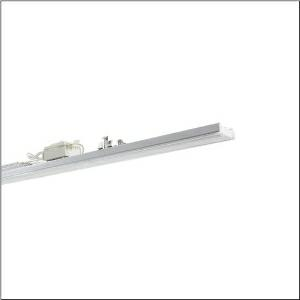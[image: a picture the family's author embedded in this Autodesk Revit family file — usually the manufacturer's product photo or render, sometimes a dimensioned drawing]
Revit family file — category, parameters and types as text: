
# Revit family: licross_r__21_recessed_mo_52tl14dn49xg_3f36
name_source: partatom
category: Lighting Fixtures
units: mm (PartAtom-declared; Revit-internal decimal feet)

## family parameters
Cut with Voids When Loaded = No
Host = Face
Light Source = No
Part Type = Normal
Room Calculation Point = No
Round Connector Dimension = Use Diameter
Shared = No

## types (1)
- --- (1 x LED, 9470 lm, 58 W, 4000K)
    Apparent Load = 58 VA
    CIE Flux Codes = 56 84 97 100 100
    Color Rendering = 80
    Color Temperature = 4000K
    Default Elevation = 1800 mm
    Description = Licross® 21 Recessed MO, luminaire insert, of sheet steel, galvanised, coil coated, white, length: 1.500mm, width: 66mm, height: 67mm, LED rated luminous flux: 9.470lm, light colour: 840, control gear: DALI 2, with plug, 5-pole, with phase selection, mains connection: 220..240V, AC, 50/60Hz, rated input power: 58W, halogen-free wiring, primary light control with lens, of plastic, primary optical cover: cover, of PMMA, light emission: direct distribution, primary light characteristic: asymmetric, protection rating (complete): IP40, insulation class (complete): insulation class I (protective earthing), certification: CE, ENEC, VDE, UKCA, protection symbol: D if used in an environment without relevant dust loads with corresponding accessories, impact resistance: IK06, permissible ambient temperature for indoor applications: -25..+35°C, corresponds to IFS (International Featured Standards) requirements for safety and quality in the food industry, reducing of maximum allowable ambient temperature of 5°C with ceiling mounting, LABS conformity tested according to VDMA 24364:2018-05, packaging unit: 1 piece
    Height = 58 mm
    Lamp = 1 x LED
    Lamp Light Flux = 9470 lm
    Lamp Power = 58 W
    Lamp count = 1
    Length = 1500 mm
    Luminous efficacy = 163 lm/W
    Manufacturer = Siteco
    ModVariant = No
    Model = 52TL14DN49XG
    Mounting Place = Ceiling
    Mounting Type = Pendant
    Number of Poles = 1
    OnlyDefault = Yes
    Power Factor = 1
    Product Name = Licross® 21 Recessed MO
    Product group = luminaire insert
    ProductGroupID = 902
    Protection Class = Protection class I
    Protection Degree = IP 40
    RLX_Detail_Level = 1
    RLX_Emergency_Light_Flux = 0 lm
    RLX_Emergency_Type = 0
    RLX_Emergency_Type_DB = No
    RlxData = <blob elided: 25037 chars, md5=971ea238>
    Socket = socket
    Standby Power = 0 W
    System Light Flux = 9470 lm
    System Power = 58 W
    Type Comments = factory setting: luminous flux: 100 % | dim-lin: 254 | 390 mA
    Type Image = l_1296930.jpg
    URL = http://relux.com
    VarID = @adj_127758
    Voltage = 0 V
    Weight = 0.00 kg
    Width = 66 mm

## geometry (parser evidence)
native form markers: Blend x4, Sweep x9
no freeform markers — native parametric forms only
